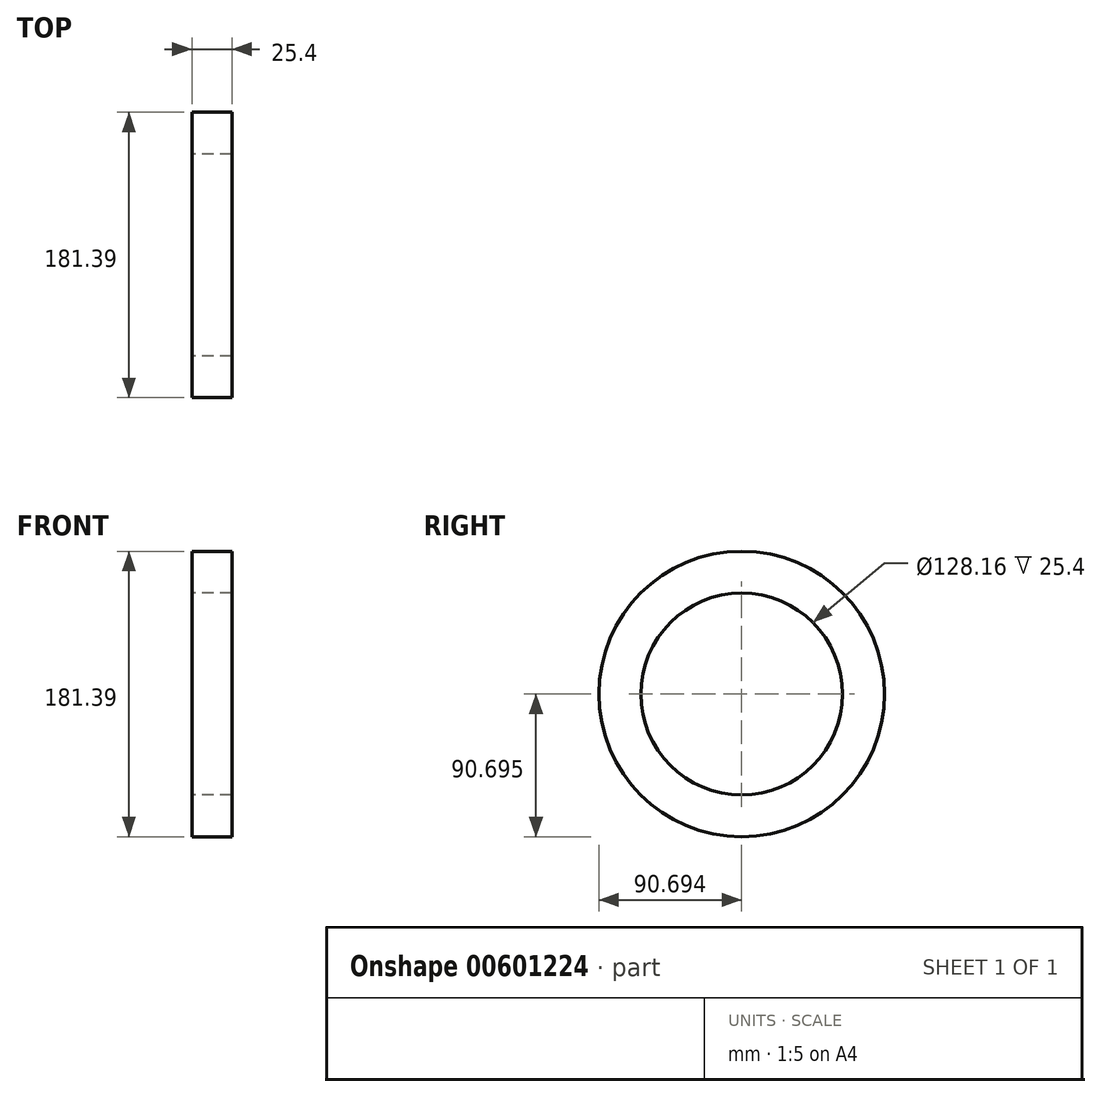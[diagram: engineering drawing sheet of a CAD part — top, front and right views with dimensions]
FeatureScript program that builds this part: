
annotation { "Feature Type Name" : "Feature", "Feature Type Description" : "" }
export const myFeature = defineFeature(function(context is Context, id is Id, definition is map)
    precondition{}
    {
        {
            var Q0;
            Q0=qCreatedBy(makeId("Right.planeOp"),FACE);
            var sketch = newSketch(context, id + "F0", { "sketchPlane" : qUnion([Q0])});
            skCircle(sketch, "E0", {"center": v(-40.72, 37.48) * mm, "radius": 90.7 * mm});
            skCircle(sketch, "E1", {"center": v(-40.72, 37.48) * mm, "radius": 64.08 * mm});
            skSolve(sketch);
        }
        {
            var Q0;
            Q0 = qSketchRegion(id + "F0", true);
            extrude(context, id + "F1", {"entities" : qUnion([Q0]), "depth" : 25.4 * mm, "offsetDistance" : 25.4 * mm});
        }
    });
